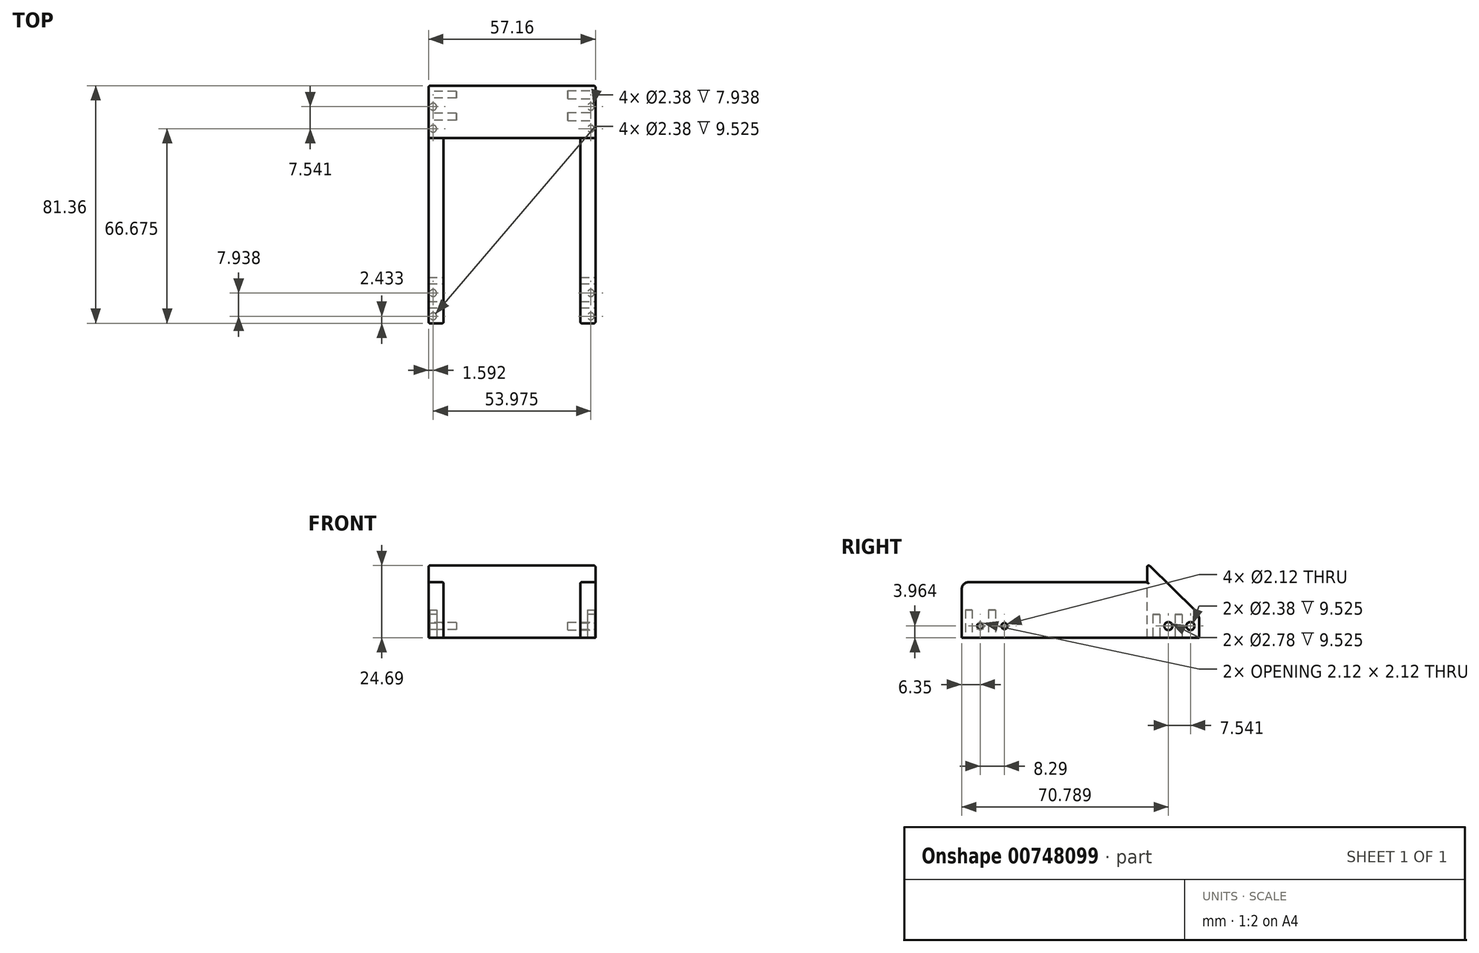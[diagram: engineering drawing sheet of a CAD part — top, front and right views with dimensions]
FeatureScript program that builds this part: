
annotation { "Feature Type Name" : "Feature", "Feature Type Description" : "" }
export const myFeature = defineFeature(function(context is Context, id is Id, definition is map)
    precondition{}
    {
        {
            var Q0;
            Q0=qCreatedBy(makeId("Top.planeOp"),FACE);
            var sketch = newSketch(context, id + "F0", { "sketchPlane" : qUnion([Q0])});
            skLineSegment(sketch, "E0.bottom", {"start": v(28.58, 8.93) * mm, "end": v(-28.58, 8.93) * mm});
            skLineSegment(sketch, "E0.top", {"start": v(28.58, -8.93) * mm, "end": v(-28.58, -8.93) * mm});
            skLineSegment(sketch, "E0.left", {"start": v(28.58, 8.93) * mm, "end": v(28.58, -8.93) * mm});
            skLineSegment(sketch, "E0.right", {"start": v(-28.58, 8.93) * mm, "end": v(-28.58, -8.93) * mm});
            skPoint(sketch, "E0.middle", {"position": v(0, 0) * mm});
            skCircle(sketch, "E1", {"center": v(-26.99, -5.75) * mm, "radius": 1.2 * mm});
            skCircle(sketch, "E2", {"center": v(-26.99, 1.79) * mm, "radius": 1.2 * mm});
            skCircle(sketch, "E3.MirrorC", {"center": v(26.99, 1.79) * mm, "radius": 1.2 * mm});
            skCircle(sketch, "E4.MirrorC", {"center": v(26.99, -5.75) * mm, "radius": 1.2 * mm});
            skSolve(sketch);
        }
        {
            var Q0;
            Q0 = qSketchRegion(id + "F0", true);
            extrude(context, id + "F1", {"entities" : qUnion([Q0]), "endBound" : BoundingType.SYMMETRIC, "depth" : 7.94 * mm, "offsetDistance" : 25.4 * mm});
        }
        {
            var Q0;
            Q0=makeQuery(id+"F1.opExtrude","SWEPT_FACE",FACE,{"disambiguationData":[OSD([sQuery(id+"F0.wireOp",EDGE,"E0.right")])]});
            var sketch = newSketch(context, id + "F2", { "sketchPlane" : qUnion([Q0])});
            skCircle(sketch, "E5", {"center": v(-5.9, 0) * mm, "radius": 1.2 * mm});
            skCircle(sketch, "E6", {"center": v(1.64, 0) * mm, "radius": 1.2 * mm});
            skLineSegment(sketch, "E7", {"start": v(8.93, 3.97) * mm, "end": v(8.93, 21.42) * mm});
            skLineSegment(sketch, "E8", {"start": v(8.93, 21.42) * mm, "end": v(-8.93, 3.97) * mm});
            skSolve(sketch);
        }
        {
            var Q0;
            Q0 = qSketchRegion(id + "F2", true);
            var Q1;
            Q1=makeQuery(id+"F1.opExtrude","SWEPT_FACE",FACE,{"disambiguationData":[OSD([sQuery(id+"F0.wireOp",EDGE,"E0.left")])]});
            extrude(context, id + "F3", {"entities" : qUnion([Q0, Q1]), "operationType" : NewBodyOperationType.REMOVE, "oppositeDirection" : true, "depth" : 9.52 * mm, "offsetDistance" : 25.4 * mm});
        }
        {
            var Q0;
            Q0=makeQuery(id+"F1.opExtrude","SWEPT_FACE",FACE,{"disambiguationData":[OSD([sQuery(id+"F0.wireOp",EDGE,"E0.left")])]});
            var sketch = newSketch(context, id + "F4", { "sketchPlane" : qUnion([Q0])});
            skCircle(sketch, "E9", {"center": v(-1.64, 0) * mm, "radius": 1.39 * mm});
            skCircle(sketch, "E10", {"center": v(5.9, 0) * mm, "radius": 1.39 * mm});
            skLineSegment(sketch, "E11", {"start": v(-8.93, 3.97) * mm, "end": v(-8.93, 21.42) * mm});
            skLineSegment(sketch, "E12", {"start": v(-8.93, 21.42) * mm, "end": v(8.93, 3.97) * mm});
            skLineSegment(sketch, "E13", {"start": v(8.93, 3.97) * mm, "end": v(-8.93, 3.97) * mm});
            skSolve(sketch);
        }
        {
            var Q0;
            Q0 = qSketchRegion(id + "F4", true);
            extrude(context, id + "F5", {"entities" : qUnion([Q0]), "operationType" : NewBodyOperationType.REMOVE, "oppositeDirection" : true, "depth" : 9.52 * mm, "offsetDistance" : 25.4 * mm});
        }
        {
            var Q0;
            Q0=makeQuery(id+"F1.opExtrude","SWEPT_FACE",FACE,{"disambiguationData":[OSD([sQuery(id+"F0.wireOp",EDGE,"E0.left")])]});
            var sketch = newSketch(context, id + "F6", { "sketchPlane" : qUnion([Q0])});
            skLineSegment(sketch, "E14", {"start": v(-8.93, 3.97) * mm, "end": v(-8.93, 21.42) * mm});
            skLineSegment(sketch, "E15", {"start": v(-8.93, 21.42) * mm, "end": v(8.93, 3.97) * mm});
            skLineSegment(sketch, "E16", {"start": v(8.93, 3.97) * mm, "end": v(-8.93, 3.97) * mm});
            skSolve(sketch);
        }
        {
            var Q0;
            Q0 = qSketchRegion(id + "F6", true);
            extrude(context, id + "F7", {"entities" : qUnion([Q0]), "operationType" : NewBodyOperationType.ADD, "depth" : -57.15 * mm, "offsetDistance" : 25.4 * mm});
        }
        {
            var Q0;
            {var subQ0=sQuery(id+"F0.wireOp",EDGE,"E0.bottom");Q0=makeQuery(id+"F7.boolean.opBoolean","MERGE",EDGE,{"derivedFrom":[makeQuery(id+"F1.opExtrude","CAP_EDGE",EDGE,{"disambiguationData":[OSD([subQ0])],"isStart":false}),makeQuery(id+"F7.opExtrude","SWEPT_EDGE",EDGE,{"disambiguationData":[OSD([subQ0,sQuery(id+"F0.wireOp",EDGE,"E0.left"),sQuery(id+"F6.wireOp",EDGE,"E15"),sQuery(id+"F6.wireOp",EDGE,"E16")])]})]});}
            fillet(context, id + "F8", {"entities" : qUnion([Q0]), "radius" : 5.08 * mm, "tangentPropagation" : true, "allowEdgeOverflow" : false});
        }
        {
            var Q0;
            Q0=makeQuery(id+"F7.boolean.opBoolean","MERGE",FACE,{"derivedFrom":[makeQuery(id+"F1.opExtrude","SWEPT_FACE",FACE,{"disambiguationData":[OSD([sQuery(id+"F0.wireOp",EDGE,"E0.top")])]}),makeQuery(id+"F7.opExtrude","SWEPT_FACE",FACE,{"disambiguationData":[OSD([sQuery(id+"F6.wireOp",EDGE,"E14")])]})]});
            var sketch = newSketch(context, id + "F9", { "sketchPlane" : qUnion([Q0])});
            skLineSegment(sketch, "E17.bottom", {"start": v(-28.58, -3.97) * mm, "end": v(-23.43, -3.97) * mm});
            skLineSegment(sketch, "E17.top", {"start": v(-28.58, 15.08) * mm, "end": v(-23.43, 15.08) * mm});
            skLineSegment(sketch, "E17.left", {"start": v(-28.58, -3.97) * mm, "end": v(-28.58, 15.08) * mm});
            skLineSegment(sketch, "E17.right", {"start": v(-23.43, -3.97) * mm, "end": v(-23.43, 15.08) * mm});
            skLineSegment(sketch, "E18.MirrorCS", {"start": v(28.58, 15.08) * mm, "end": v(23.43, 15.08) * mm});
            skLineSegment(sketch, "E19.MirrorCS", {"start": v(28.58, -3.97) * mm, "end": v(28.58, 15.08) * mm});
            skLineSegment(sketch, "E20.MirrorCS", {"start": v(28.58, -3.97) * mm, "end": v(23.43, -3.97) * mm});
            skLineSegment(sketch, "E21.MirrorCS", {"start": v(23.43, -3.97) * mm, "end": v(23.43, 15.08) * mm});
            skSolve(sketch);
        }
        {
            var Q0;
            Q0 = qSketchRegion(id + "F9", true);
            extrude(context, id + "F10", {"entities" : qUnion([Q0]), "operationType" : NewBodyOperationType.ADD, "depth" : 63.5 * mm, "offsetDistance" : 25.4 * mm});
        }
        {
            var Q0;
            Q0=makeQuery(id+"F10.boolean.opBoolean","MERGE",FACE,{"derivedFrom":[makeQuery(id+"F7.boolean.opBoolean","MERGE",FACE,{"derivedFrom":[makeQuery(id+"F1.opExtrude","SWEPT_FACE",FACE,{"disambiguationData":[OSD([sQuery(id+"F0.wireOp",EDGE,"E0.left")])]}),makeQuery(id+"F7.opExtrude","CAP_FACE",FACE,{"disambiguationData":[OSD([sQuery(id+"F6.wireOp",EDGE,"E14"),sQuery(id+"F6.wireOp",EDGE,"E15"),sQuery(id+"F6.wireOp",EDGE,"E16")])],"isStart":true})]}),makeQuery(id+"F10.opExtrude","SWEPT_FACE",FACE,{"disambiguationData":[OSD([sQuery(id+"F9.wireOp",EDGE,"E19.MirrorCS")])]})]});
            var sketch = newSketch(context, id + "F11", { "sketchPlane" : qUnion([Q0])});
            skCircle(sketch, "E22", {"center": v(-66.08, 0) * mm, "radius": 1.06 * mm});
            skCircle(sketch, "E23", {"center": v(-57.79, 0) * mm, "radius": 1.06 * mm});
            skSolve(sketch);
        }
        {
            var Q0;
            Q0 = qSketchRegion(id + "F11", true);
            extrude(context, id + "F12", {"entities" : qUnion([Q0]), "operationType" : NewBodyOperationType.REMOVE, "oppositeDirection" : true, "depth" : 57.15 * mm, "offsetDistance" : 25.4 * mm});
        }
        {
            var Q0;
            Q0=makeQuery(id+"F10.boolean.opBoolean","MERGE",FACE,{"derivedFrom":[makeQuery(id+"F1.opExtrude","CAP_FACE",FACE,{"disambiguationData":[OSD([sQuery(id+"F0.wireOp",EDGE,"E0.bottom"),sQuery(id+"F0.wireOp",EDGE,"E0.top"),sQuery(id+"F0.wireOp",EDGE,"E0.left"),sQuery(id+"F0.wireOp",EDGE,"E0.right"),sQuery(id+"F0.wireOp",EDGE,"E1"),sQuery(id+"F0.wireOp",EDGE,"E2"),sQuery(id+"F0.wireOp",EDGE,"E3.MirrorC"),sQuery(id+"F0.wireOp",EDGE,"E4.MirrorC")])],"isStart":true}),makeQuery(id+"F10.opExtrude","SWEPT_FACE",FACE,{"disambiguationData":[OSD([sQuery(id+"F9.wireOp",EDGE,"E17.bottom")])]}),makeQuery(id+"F10.opExtrude","SWEPT_FACE",FACE,{"disambiguationData":[OSD([sQuery(id+"F9.wireOp",EDGE,"E20.MirrorCS")])]})]});
            var sketch = newSketch(context, id + "F13", { "sketchPlane" : qUnion([Q0])});
            skCircle(sketch, "E24", {"center": v(26.99, 70) * mm, "radius": 1.2 * mm});
            skCircle(sketch, "E25", {"center": v(26.99, 62.06) * mm, "radius": 1.2 * mm});
            skCircle(sketch, "E26", {"center": v(-26.99, 70) * mm, "radius": 1.2 * mm});
            skCircle(sketch, "E27", {"center": v(-26.99, 62.06) * mm, "radius": 1.2 * mm});
            skSolve(sketch);
        }
        {
            var Q0;
            Q0 = qSketchRegion(id + "F13", true);
            extrude(context, id + "F14", {"entities" : qUnion([Q0]), "operationType" : NewBodyOperationType.REMOVE, "oppositeDirection" : true, "depth" : 9.52 * mm, "offsetDistance" : 25.4 * mm});
        }
        {
            var Q0;
            Q0=makeQuery(id+"F7.opExtrude","SWEPT_EDGE",EDGE,{"disambiguationData":[OSD([sQuery(id+"F6.wireOp",EDGE,"E14"),sQuery(id+"F6.wireOp",EDGE,"E15")])]});
            var Q1;
            Q1=makeQuery(id+"F10.opExtrude","SWEPT_EDGE",EDGE,{"disambiguationData":[OSD([sQuery(id+"F0.wireOp",EDGE,"E0.top"),sQuery(id+"F0.wireOp",EDGE,"E0.left"),sQuery(id+"F6.wireOp",EDGE,"E14"),sQuery(id+"F9.wireOp",EDGE,"E18.MirrorCS"),sQuery(id+"F9.wireOp",EDGE,"E19.MirrorCS")])]});
            var Q2;
            Q2=makeQuery(id+"F10.opExtrude","SWEPT_EDGE",EDGE,{"disambiguationData":[OSD([sQuery(id+"F9.wireOp",EDGE,"E18.MirrorCS"),sQuery(id+"F9.wireOp",EDGE,"E21.MirrorCS")])]});
            var Q3;
            Q3=makeQuery(id+"F10.opExtrude","SWEPT_EDGE",EDGE,{"disambiguationData":[OSD([sQuery(id+"F9.wireOp",EDGE,"E17.top"),sQuery(id+"F9.wireOp",EDGE,"E17.right")])]});
            var Q4;
            Q4=makeQuery(id+"F10.opExtrude","SWEPT_EDGE",EDGE,{"disambiguationData":[OSD([sQuery(id+"F0.wireOp",EDGE,"E0.top"),sQuery(id+"F0.wireOp",EDGE,"E0.right"),sQuery(id+"F6.wireOp",EDGE,"E14"),sQuery(id+"F9.wireOp",EDGE,"E17.top"),sQuery(id+"F9.wireOp",EDGE,"E17.left")])]});
            var Q5;
            Q5=makeQuery(id+"F10.opExtrude","CAP_EDGE",EDGE,{"disambiguationData":[OSD([sQuery(id+"F9.wireOp",EDGE,"E19.MirrorCS")])],"isStart":false});
            var Q6;
            Q6=makeQuery(id+"F10.opExtrude","CAP_EDGE",EDGE,{"disambiguationData":[OSD([sQuery(id+"F9.wireOp",EDGE,"E17.right")])],"isStart":false});
            var Q7;
            Q7=makeQuery(id+"F10.opExtrude","CAP_EDGE",EDGE,{"disambiguationData":[OSD([sQuery(id+"F9.wireOp",EDGE,"E17.left")])],"isStart":false});
            var Q8;
            Q8=makeQuery(id+"F10.opExtrude","CAP_EDGE",EDGE,{"disambiguationData":[OSD([sQuery(id+"F9.wireOp",EDGE,"E21.MirrorCS")])],"isStart":false});
            fillet(context, id + "F15", {"entities" : qUnion([Q0, Q1, Q2, Q3, Q4, Q5, Q6, Q7, Q8]), "radius" : 0.5 * mm, "tangentPropagation" : true, "allowEdgeOverflow" : false});
        }
        {
            var Q0;
            Q0=makeQuery(id+"F10.opExtrude","CAP_EDGE",EDGE,{"disambiguationData":[OSD([sQuery(id+"F9.wireOp",EDGE,"E17.top")])],"isStart":true});
            var Q1;
            Q1=makeQuery(id+"F10.opExtrude","CAP_EDGE",EDGE,{"disambiguationData":[OSD([sQuery(id+"F9.wireOp",EDGE,"E18.MirrorCS")])],"isStart":true});
            var Q2;
            Q2=makeQuery(id+"F10.opExtrude","CAP_EDGE",EDGE,{"disambiguationData":[OSD([sQuery(id+"F9.wireOp",EDGE,"E17.top")])],"isStart":false});
            var Q3;
            Q3=makeQuery(id+"F10.opExtrude","CAP_EDGE",EDGE,{"disambiguationData":[OSD([sQuery(id+"F9.wireOp",EDGE,"E18.MirrorCS")])],"isStart":false});
            fillet(context, id + "F16", {"entities" : qUnion([Q0, Q1, Q2, Q3]), "radius" : 2.54 * mm, "tangentPropagation" : true, "allowEdgeOverflow" : false});
        }
        {
            var Q0;
            Q0=makeQuery(id+"F1.opExtrude","SWEPT_EDGE",EDGE,{"disambiguationData":[OSD([sQuery(id+"F0.wireOp",EDGE,"E0.bottom"),sQuery(id+"F0.wireOp",EDGE,"E0.left")])]});
            var Q1;
            Q1=makeQuery(id+"F1.opExtrude","SWEPT_EDGE",EDGE,{"disambiguationData":[OSD([sQuery(id+"F0.wireOp",EDGE,"E0.bottom"),sQuery(id+"F0.wireOp",EDGE,"E0.right")])]});
            var Q2;
            Q2=makeQuery(id+"F7.opExtrude","CAP_EDGE",EDGE,{"disambiguationData":[OSD([sQuery(id+"F6.wireOp",EDGE,"E15")])],"isStart":false});
            var Q3;
            Q3=makeQuery(id+"F7.opExtrude","CAP_EDGE",EDGE,{"disambiguationData":[OSD([sQuery(id+"F6.wireOp",EDGE,"E15")])],"isStart":true});
            fillet(context, id + "F17", {"entities" : qUnion([Q0, Q1, Q2, Q3]), "radius" : 0.5 * mm, "tangentPropagation" : true, "allowEdgeOverflow" : false});
        }
    });
